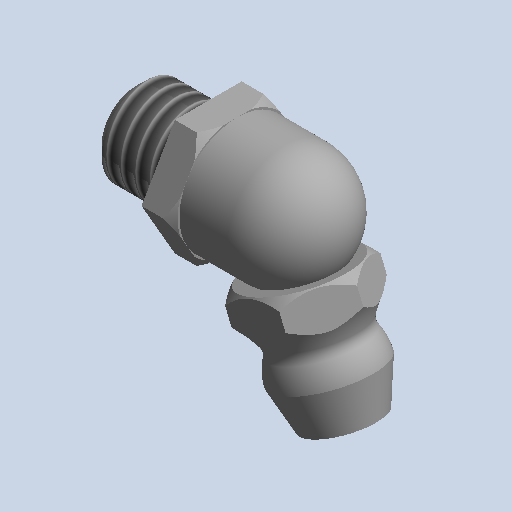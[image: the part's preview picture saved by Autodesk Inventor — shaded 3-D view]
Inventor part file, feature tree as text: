
AUTODESK INVENTOR PART (.ipt)
format: ipt  version: 2022 (Build 260153000, 153)  size: 226,304 bytes
history: native  units: mm (DEFAULTED — no unit token found)
features: other x7, sketch x5, revolve x3, extrude x2, thread x1
ambient origin geometry x8: Origin, YZ Plane, XZ Plane, XY Plane, X Axis, Y Axis, Z Axis, Center Point
bodies: Solid1 (feature_tree)
feature tree (18):
  revolve  "Revolution1"  [1 undecoded]
  thread  "Thread1"  [1 undecoded]
  revolve  "Revolution2"  Angle=360.0deg
  extrude  "Extrusion1"  TaperAngle=0.0deg  [1 undecoded]
  revolve  "Revolution3"  [1 undecoded]
  extrude  "Extrusion2"  [1 undecoded]
  other  "n_j_XY"
  other  "n_j_YZ"
  other  "n_j_ZX"
  other  "n_j_X"
  other  "n_j_Y"
  other  "n_j_Z"
  other  "n_j_Center"
  sketch  "Sketch_1"  dims[d0=360.0deg d1=3.84338mm d2=0.0mm d3=360.0deg]
  sketch  "Sketch_5"  dims[d4=5.0mm d5=0.0mm d6=360.0deg]
  sketch  "Sketch_13"  dims[d7=2.5mm d8=0.0mm d9=0.0mm]
  sketch  "Sketch_17"
  sketch  "Sketch_18"
note: 5 required parameter values undecoded (feature->parameter linkage not recoverable at this tier; creation-order binding heuristic only, values carry confidence <= 0.55)